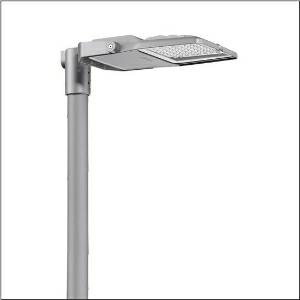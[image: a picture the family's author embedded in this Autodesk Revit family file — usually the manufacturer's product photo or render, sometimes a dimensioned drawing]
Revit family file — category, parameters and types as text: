
# Revit family: floodlight_fl_21_mini___pl52_5xa7776c4d3a_f656
name_source: partatom
category: Lighting Fixtures
units: mm (PartAtom-declared; Revit-internal decimal feet)

## family parameters
Cut with Voids When Loaded = No
Host = Face
Light Source = No
Part Type = Normal
Room Calculation Point = No
Round Connector Dimension = Use Diameter
Shared = No

## types (1)
- --- (1 x LED, 12700 lm, 89 W, 4000K)
    Apparent Load = 89 VA
    CIE Flux Codes = 26 60 98 100 100
    Color Rendering = 70
    Color Temperature = 4000K
    Default Elevation = 1800 mm
    Description = Floodlight FL 21 mini, floodlight, primary light control with lens, of PMMA, primary optical cover: protective disc, of toughened safety glass, transparent, light distribution: PL52, light emission: direct distribution, installation type: surface-mounted, LED, High Power LED, rated luminous flux: 12.700lm, luminous efficacy: 143lm/W, light colour: 740, colour temperature: 4000K, control gear: Smart Interface (Zhaga), control: pre-setting: logarithmic dimming characteristic, flexible luminous flux parameterisation, time-dependent luminous flux control, constant luminous flux control, overheat protection, with terminal, 6-pole, mains connection: 220..240V, AC, 50/60Hz, start of lifetime: 89W, end of service life: 94W, reduction: 43W, luminaire housing, of diecast aluminium, powder-coated, Siteco® metallic grey (DB 702S), corrosivity category C5 mid according to DIN EN ISO 12944, suitable for swimming pools, chlorine-resistant, sealing non-destructively replaceable, please order mast flange separately, mast bracket, of steel, galvanised, powder-coated, Siteco® metallic grey (DB 702S), Smart Interface below and above, protection rating (complete): IP66, insulation class (complete): insulation class II (safety insulation), certification: CE, ENEC, VDE, protection symbol: D, impact resistance: IK08, permissible operating ambient temperature: -40..+40°C, permissible operating ambient temperature for outdoor applications: -40..+50°C, standard: DIN EN 12944, LABS conformity tested according to VDMA 24364:2018-05, packaging unit: 1 piece

Light Distribution: PL52
    Height = 70 mm
    Lamp = 1 x LED
    Lamp Light Flux = 12700 lm
    Lamp Power = 89 W
    Lamp count = 1
    Length = 485 mm
    Luminous efficacy = 143 lm/W
    Manufacturer = Siteco
    ModVariant = No
    Model = 5XA7776C4D3A
    Number of Poles = 1
    OnlyDefault = Yes
    Power Factor = 1
    Product Name = Floodlight FL 21 mini | PL52
    Product group = floodlight | pylon annexe
    ProductGroupID = 6201
    Protection Class = Protection class II
    Protection Degree = IP 66
    RLX_Detail_Level = 1
    RLX_Emergency_Light_Flux = 0 lm
    RLX_Emergency_Type = 0
    RLX_Emergency_Type_DB = No
    RlxData = <blob elided: 101205 chars, md5=fa3030bb>
    Socket = socket
    Standby Power = 0 W
    System Light Flux = 12700 lm
    System Power = 89 W
    Type Comments = factory setting: luminous flux: 100 % | dim-lin: 254 | 456 mA
    Type Image = l_1007125.jpg
    URL = http://relux.com
    VarID = @adj_047153
    Voltage = 0 V
    Weight = 0.00 kg
    Width = 337 mm

## geometry (parser evidence)
native form markers: Blend x4, Sweep x12
no freeform markers — native parametric forms only
